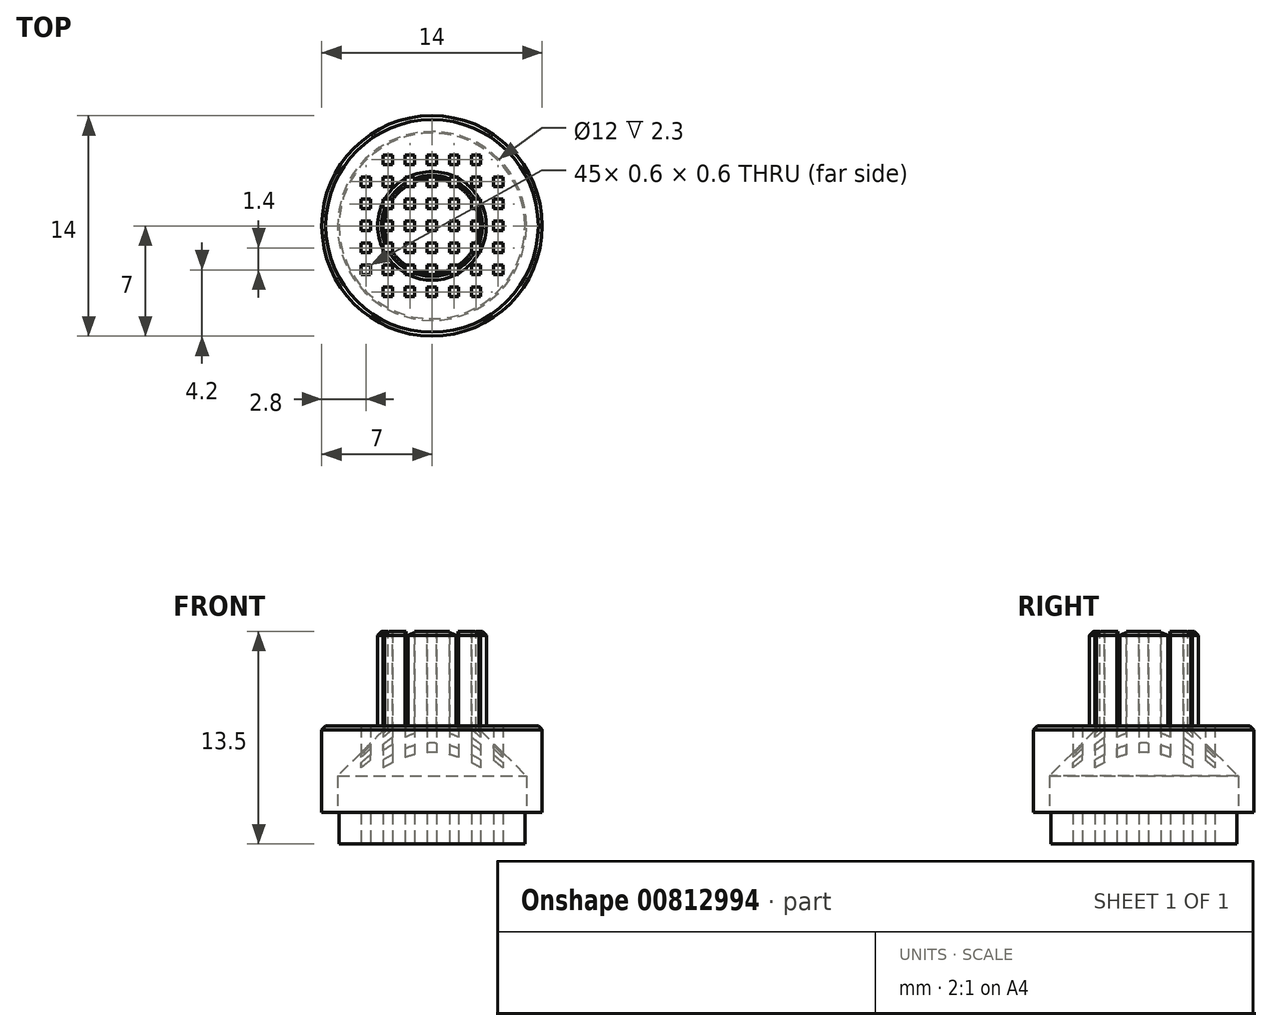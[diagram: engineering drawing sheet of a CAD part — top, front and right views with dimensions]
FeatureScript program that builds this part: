
annotation { "Feature Type Name" : "Feature", "Feature Type Description" : "" }
export const myFeature = defineFeature(function(context is Context, id is Id, definition is map)
    precondition{}
    {
        {
            var Q0;
            Q0=qCreatedBy(makeId("Top.planeOp"),FACE);
            var sketch = newSketch(context, id + "F0", { "sketchPlane" : qUnion([Q0])});
            skCircle(sketch, "E0", {"center": v(0, 0) * mm, "radius": 7 * mm});
            skSolve(sketch);
        }
        {
            var Q0;
            Q0 = qSketchRegion(id + "F0", true);
            extrude(context, id + "F1", {"entities" : qUnion([Q0]), "depth" : 5.5 * mm, "offsetDistance" : 25 * mm});
        }
        {
            var Q0;
            Q0=makeQuery(id+"F1.opExtrude","CAP_FACE",FACE,{"disambiguationData":[OSD([sQuery(id+"F0.wireOp",EDGE,"E0")])],"isStart":false});
            var sketch = newSketch(context, id + "F2", { "sketchPlane" : qUnion([Q0])});
            skCircle(sketch, "E1", {"center": v(0, 0) * mm, "radius": 3.45 * mm});
            skSolve(sketch);
        }
        {
            var Q0;
            Q0=makeQuery(id+"F2.imprint","IMPRINT",FACE,{"disambiguationData":[TD([[makeQuery(id+"F2.imprint","IMPRINT",EDGE,{"derivedFrom":sQuery(id+"F2.wireOp",EDGE,"E1")}),1.0]])]});
            extrude(context, id + "F3", {"entities" : qUnion([Q0]), "operationType" : NewBodyOperationType.ADD, "depth" : 6 * mm, "offsetDistance" : 25 * mm});
        }
        {
            var Q0;
            Q0=makeQuery(id+"F3.opExtrude","CAP_FACE",FACE,{"disambiguationData":[OSD([sQuery(id+"F2.wireOp",EDGE,"E1")])],"isStart":false});
            var sketch = newSketch(context, id + "F4", { "sketchPlane" : qUnion([Q0])});
            skCircle(sketch, "E2", {"center": v(0, 0) * mm, "radius": 3 * mm});
            skSolve(sketch);
        }
        {
            var Q0;
            Q0=makeQuery(id+"F4.imprint","IMPRINT",FACE,{"disambiguationData":[TD([[makeQuery(id+"F4.imprint","IMPRINT",EDGE,{"derivedFrom":sQuery(id+"F4.wireOp",EDGE,"E2")}),1.0]])]});
            extrude(context, id + "F5", {"entities" : qUnion([Q0]), "operationType" : NewBodyOperationType.REMOVE, "oppositeDirection" : true, "depth" : 25 * mm, "offsetDistance" : 25 * mm});
        }
        {
            var Q0;
            Q0=makeQuery(id+"F1.opExtrude","CAP_FACE",FACE,{"disambiguationData":[OSD([sQuery(id+"F0.wireOp",EDGE,"E0")])],"isStart":true});
            var sketch = newSketch(context, id + "F6", { "sketchPlane" : qUnion([Q0])});
            skCircle(sketch, "E3", {"center": v(0, 0) * mm, "radius": 6 * mm});
            skSolve(sketch);
        }
        {
            var Q0;
            Q0=makeQuery(id+"F6.imprint","IMPRINT",FACE,{"disambiguationData":[TD([[makeQuery(id+"F6.imprint","IMPRINT",EDGE,{"derivedFrom":makeQuery(id+"F5.boolean.opBoolean","INTERSECT",EDGE,{"derivedFrom":[makeQuery(id+"F1.opExtrude","CAP_FACE",FACE,{"disambiguationData":[OSD([sQuery(id+"F0.wireOp",EDGE,"E0")])],"isStart":true}),makeQuery(id+"F5.opExtrude","SWEPT_FACE",FACE,{"disambiguationData":[OSD([sQuery(id+"F4.wireOp",EDGE,"E2")])]})]})}),-1.0]])]});
            var Q1;
            Q1=makeQuery(id+"F6.imprint","IMPRINT",FACE,{"disambiguationData":[TD([[makeQuery(id+"F6.imprint","IMPRINT",EDGE,{"derivedFrom":sQuery(id+"F6.wireOp",EDGE,"E3")}),1.0]])]});
            extrude(context, id + "F7", {"entities" : qUnion([Q0, Q1]), "operationType" : NewBodyOperationType.REMOVE, "oppositeDirection" : true, "depth" : 2 * mm, "offsetDistance" : 25 * mm});
        }
        {
            var Q0;
            Q0=makeQuery(id+"F7.boolean.opBoolean","INTERSECT",EDGE,{"derivedFrom":[makeQuery(id+"F5.boolean.opBoolean","COPY",FACE,{"derivedFrom":makeQuery(id+"F5.opExtrude","SWEPT_FACE",FACE,{"disambiguationData":[OSD([sQuery(id+"F4.wireOp",EDGE,"E2")])]})}),makeQuery(id+"F7.opExtrude","CAP_FACE",FACE,{"disambiguationData":[OSD([sQuery(id+"F6.wireOp",EDGE,"E3")])],"isStart":false})]});
            chamfer(context, id + "F8", {"entities" : qUnion([Q0]), "width" : 3.3 * mm, "tangentPropagation" : true});
        }
        {
            var Q0;
            Q0=makeQuery(id+"F3.opExtrude","CAP_EDGE",EDGE,{"disambiguationData":[OSD([sQuery(id+"F2.wireOp",EDGE,"E1")])],"isStart":false});
            var Q1;
            Q1=makeQuery(id+"F1.opExtrude","CAP_EDGE",EDGE,{"disambiguationData":[OSD([sQuery(id+"F0.wireOp",EDGE,"E0")])],"isStart":false});
            chamfer(context, id + "F9", {"entities" : qUnion([Q0, Q1]), "width" : 0.25 * mm, "tangentPropagation" : true});
        }
        {
            var Q0;
            Q0=qCreatedBy(makeId("Top.planeOp"),FACE);
            var sketch = newSketch(context, id + "F10", { "sketchPlane" : qUnion([Q0])});
            skCircle(sketch, "E4", {"center": v(0, 0) * mm, "radius": 5.9 * mm});
            skSolve(sketch);
        }
        {
            var Q0;
            Q0=makeQuery(id+"F10.imprint","IMPRINT",FACE,{"disambiguationData":[TD([[makeQuery(id+"F10.imprint","IMPRINT",EDGE,{"derivedFrom":sQuery(id+"F10.wireOp",EDGE,"E4")}),1.0]])]});
            extrude(context, id + "F11", {"entities" : qUnion([Q0]), "operationType" : NewBodyOperationType.ADD, "oppositeDirection" : true, "depth" : 2 * mm, "offsetDistance" : 25 * mm});
        }
        {
            var Q0;
            Q0=makeQuery(id+"F11.opExtrude","CAP_FACE",FACE,{"disambiguationData":[OSD([sQuery(id+"F10.wireOp",EDGE,"E4")])],"isStart":false});
            var sketch = newSketch(context, id + "F12", { "sketchPlane" : qUnion([Q0])});
            skLineSegment(sketch, "E5.bottom", {"start": v(-5.3, -5.9) * mm, "end": v(-5.9, -5.9) * mm});
            skLineSegment(sketch, "E5.top", {"start": v(-5.3, -5.3) * mm, "end": v(-5.9, -5.3) * mm});
            skLineSegment(sketch, "E5.left", {"start": v(-5.3, -5.9) * mm, "end": v(-5.3, -5.3) * mm});
            skLineSegment(sketch, "E5.right", {"start": v(-5.9, -5.9) * mm, "end": v(-5.9, -5.3) * mm});
            skPoint(sketch, "E5.middle", {"position": v(-5.6, -5.6) * mm});
            skPoint(sketch, "E6.1.2.0", {"position": v(-4.2, -2.8) * mm});
            skLineSegment(sketch, "E6.1.2.1", {"start": v(-3.9, -3.1) * mm, "end": v(-4.5, -3.1) * mm});
            skLineSegment(sketch, "E6.1.2.2", {"start": v(-3.9, -2.5) * mm, "end": v(-4.5, -2.5) * mm});
            skLineSegment(sketch, "E6.1.2.3", {"start": v(-3.9, -3.1) * mm, "end": v(-3.9, -2.5) * mm});
            skLineSegment(sketch, "E6.1.2.4", {"start": v(-4.5, -3.1) * mm, "end": v(-4.5, -2.5) * mm});
            skPoint(sketch, "E6.1.3.0", {"position": v(-4.2, -1.4) * mm});
            skLineSegment(sketch, "E6.1.3.1", {"start": v(-3.9, -1.7) * mm, "end": v(-4.5, -1.7) * mm});
            skLineSegment(sketch, "E6.1.3.2", {"start": v(-3.9, -1.1) * mm, "end": v(-4.5, -1.1) * mm});
            skLineSegment(sketch, "E6.1.3.3", {"start": v(-3.9, -1.7) * mm, "end": v(-3.9, -1.1) * mm});
            skLineSegment(sketch, "E6.1.3.4", {"start": v(-4.5, -1.7) * mm, "end": v(-4.5, -1.1) * mm});
            skPoint(sketch, "E6.1.4.0", {"position": v(-4.2, 0) * mm});
            skLineSegment(sketch, "E6.1.4.1", {"start": v(-3.9, -0.3) * mm, "end": v(-4.5, -0.3) * mm});
            skLineSegment(sketch, "E6.1.4.2", {"start": v(-3.9, 0.3) * mm, "end": v(-4.5, 0.3) * mm});
            skLineSegment(sketch, "E6.1.4.3", {"start": v(-3.9, -0.3) * mm, "end": v(-3.9, 0.3) * mm});
            skLineSegment(sketch, "E6.1.4.4", {"start": v(-4.5, -0.3) * mm, "end": v(-4.5, 0.3) * mm});
            skPoint(sketch, "E6.1.5.0", {"position": v(-4.2, 1.4) * mm});
            skLineSegment(sketch, "E6.1.5.1", {"start": v(-3.9, 1.1) * mm, "end": v(-4.5, 1.1) * mm});
            skLineSegment(sketch, "E6.1.5.2", {"start": v(-3.9, 1.7) * mm, "end": v(-4.5, 1.7) * mm});
            skLineSegment(sketch, "E6.1.5.3", {"start": v(-3.9, 1.1) * mm, "end": v(-3.9, 1.7) * mm});
            skLineSegment(sketch, "E6.1.5.4", {"start": v(-4.5, 1.1) * mm, "end": v(-4.5, 1.7) * mm});
            skPoint(sketch, "E6.1.6.0", {"position": v(-4.2, 2.8) * mm});
            skLineSegment(sketch, "E6.1.6.1", {"start": v(-3.9, 2.5) * mm, "end": v(-4.5, 2.5) * mm});
            skLineSegment(sketch, "E6.1.6.2", {"start": v(-3.9, 3.1) * mm, "end": v(-4.5, 3.1) * mm});
            skLineSegment(sketch, "E6.1.6.3", {"start": v(-3.9, 2.5) * mm, "end": v(-3.9, 3.1) * mm});
            skLineSegment(sketch, "E6.1.6.4", {"start": v(-4.5, 2.5) * mm, "end": v(-4.5, 3.1) * mm});
            skPoint(sketch, "E6.2.1.0", {"position": v(-2.8, -4.2) * mm});
            skLineSegment(sketch, "E6.2.1.1", {"start": v(-2.5, -4.5) * mm, "end": v(-3.1, -4.5) * mm});
            skLineSegment(sketch, "E6.2.1.2", {"start": v(-2.5, -3.9) * mm, "end": v(-3.1, -3.9) * mm});
            skLineSegment(sketch, "E6.2.1.3", {"start": v(-2.5, -4.5) * mm, "end": v(-2.5, -3.9) * mm});
            skLineSegment(sketch, "E6.2.1.4", {"start": v(-3.1, -4.5) * mm, "end": v(-3.1, -3.9) * mm});
            skPoint(sketch, "E6.2.2.0", {"position": v(-2.8, -2.8) * mm});
            skLineSegment(sketch, "E6.2.2.1", {"start": v(-2.5, -3.1) * mm, "end": v(-3.1, -3.1) * mm});
            skLineSegment(sketch, "E6.2.2.2", {"start": v(-2.5, -2.5) * mm, "end": v(-3.1, -2.5) * mm});
            skLineSegment(sketch, "E6.2.2.3", {"start": v(-2.5, -3.1) * mm, "end": v(-2.5, -2.5) * mm});
            skLineSegment(sketch, "E6.2.2.4", {"start": v(-3.1, -3.1) * mm, "end": v(-3.1, -2.5) * mm});
            skPoint(sketch, "E6.2.3.0", {"position": v(-2.8, -1.4) * mm});
            skLineSegment(sketch, "E6.2.3.1", {"start": v(-2.5, -1.7) * mm, "end": v(-3.1, -1.7) * mm});
            skLineSegment(sketch, "E6.2.3.2", {"start": v(-2.5, -1.1) * mm, "end": v(-3.1, -1.1) * mm});
            skLineSegment(sketch, "E6.2.3.3", {"start": v(-2.5, -1.7) * mm, "end": v(-2.5, -1.1) * mm});
            skLineSegment(sketch, "E6.2.3.4", {"start": v(-3.1, -1.7) * mm, "end": v(-3.1, -1.1) * mm});
            skPoint(sketch, "E6.2.4.0", {"position": v(-2.8, 0) * mm});
            skLineSegment(sketch, "E6.2.4.1", {"start": v(-2.5, -0.3) * mm, "end": v(-3.1, -0.3) * mm});
            skLineSegment(sketch, "E6.2.4.2", {"start": v(-2.5, 0.3) * mm, "end": v(-3.1, 0.3) * mm});
            skLineSegment(sketch, "E6.2.4.3", {"start": v(-2.5, -0.3) * mm, "end": v(-2.5, 0.3) * mm});
            skLineSegment(sketch, "E6.2.4.4", {"start": v(-3.1, -0.3) * mm, "end": v(-3.1, 0.3) * mm});
            skPoint(sketch, "E6.2.5.0", {"position": v(-2.8, 1.4) * mm});
            skLineSegment(sketch, "E6.2.5.1", {"start": v(-2.5, 1.1) * mm, "end": v(-3.1, 1.1) * mm});
            skLineSegment(sketch, "E6.2.5.2", {"start": v(-2.5, 1.7) * mm, "end": v(-3.1, 1.7) * mm});
            skLineSegment(sketch, "E6.2.5.3", {"start": v(-2.5, 1.1) * mm, "end": v(-2.5, 1.7) * mm});
            skLineSegment(sketch, "E6.2.5.4", {"start": v(-3.1, 1.1) * mm, "end": v(-3.1, 1.7) * mm});
            skPoint(sketch, "E6.2.6.0", {"position": v(-2.8, 2.8) * mm});
            skLineSegment(sketch, "E6.2.6.1", {"start": v(-2.5, 2.5) * mm, "end": v(-3.1, 2.5) * mm});
            skLineSegment(sketch, "E6.2.6.2", {"start": v(-2.5, 3.1) * mm, "end": v(-3.1, 3.1) * mm});
            skLineSegment(sketch, "E6.2.6.3", {"start": v(-2.5, 2.5) * mm, "end": v(-2.5, 3.1) * mm});
            skLineSegment(sketch, "E6.2.6.4", {"start": v(-3.1, 2.5) * mm, "end": v(-3.1, 3.1) * mm});
            skPoint(sketch, "E6.2.7.0", {"position": v(-2.8, 4.2) * mm});
            skLineSegment(sketch, "E6.2.7.1", {"start": v(-2.5, 3.9) * mm, "end": v(-3.1, 3.9) * mm});
            skLineSegment(sketch, "E6.2.7.2", {"start": v(-2.5, 4.5) * mm, "end": v(-3.1, 4.5) * mm});
            skLineSegment(sketch, "E6.2.7.3", {"start": v(-2.5, 3.9) * mm, "end": v(-2.5, 4.5) * mm});
            skLineSegment(sketch, "E6.2.7.4", {"start": v(-3.1, 3.9) * mm, "end": v(-3.1, 4.5) * mm});
            skPoint(sketch, "E6.3.1.0", {"position": v(-1.4, -4.2) * mm});
            skLineSegment(sketch, "E6.3.1.1", {"start": v(-1.1, -4.5) * mm, "end": v(-1.7, -4.5) * mm});
            skLineSegment(sketch, "E6.3.1.2", {"start": v(-1.1, -3.9) * mm, "end": v(-1.7, -3.9) * mm});
            skLineSegment(sketch, "E6.3.1.3", {"start": v(-1.1, -4.5) * mm, "end": v(-1.1, -3.9) * mm});
            skLineSegment(sketch, "E6.3.1.4", {"start": v(-1.7, -4.5) * mm, "end": v(-1.7, -3.9) * mm});
            skPoint(sketch, "E6.3.2.0", {"position": v(-1.4, -2.8) * mm});
            skLineSegment(sketch, "E6.3.2.1", {"start": v(-1.1, -3.1) * mm, "end": v(-1.7, -3.1) * mm});
            skLineSegment(sketch, "E6.3.2.2", {"start": v(-1.1, -2.5) * mm, "end": v(-1.7, -2.5) * mm});
            skLineSegment(sketch, "E6.3.2.3", {"start": v(-1.1, -3.1) * mm, "end": v(-1.1, -2.5) * mm});
            skLineSegment(sketch, "E6.3.2.4", {"start": v(-1.7, -3.1) * mm, "end": v(-1.7, -2.5) * mm});
            skPoint(sketch, "E6.3.3.0", {"position": v(-1.4, -1.4) * mm});
            skLineSegment(sketch, "E6.3.3.1", {"start": v(-1.1, -1.7) * mm, "end": v(-1.7, -1.7) * mm});
            skLineSegment(sketch, "E6.3.3.2", {"start": v(-1.1, -1.1) * mm, "end": v(-1.7, -1.1) * mm});
            skLineSegment(sketch, "E6.3.3.3", {"start": v(-1.1, -1.7) * mm, "end": v(-1.1, -1.1) * mm});
            skLineSegment(sketch, "E6.3.3.4", {"start": v(-1.7, -1.7) * mm, "end": v(-1.7, -1.1) * mm});
            skPoint(sketch, "E6.3.4.0", {"position": v(-1.4, 0) * mm});
            skLineSegment(sketch, "E6.3.4.1", {"start": v(-1.1, -0.3) * mm, "end": v(-1.7, -0.3) * mm});
            skLineSegment(sketch, "E6.3.4.2", {"start": v(-1.1, 0.3) * mm, "end": v(-1.7, 0.3) * mm});
            skLineSegment(sketch, "E6.3.4.3", {"start": v(-1.1, -0.3) * mm, "end": v(-1.1, 0.3) * mm});
            skLineSegment(sketch, "E6.3.4.4", {"start": v(-1.7, -0.3) * mm, "end": v(-1.7, 0.3) * mm});
            skPoint(sketch, "E6.3.5.0", {"position": v(-1.4, 1.4) * mm});
            skLineSegment(sketch, "E6.3.5.1", {"start": v(-1.1, 1.1) * mm, "end": v(-1.7, 1.1) * mm});
            skLineSegment(sketch, "E6.3.5.2", {"start": v(-1.1, 1.7) * mm, "end": v(-1.7, 1.7) * mm});
            skLineSegment(sketch, "E6.3.5.3", {"start": v(-1.1, 1.1) * mm, "end": v(-1.1, 1.7) * mm});
            skLineSegment(sketch, "E6.3.5.4", {"start": v(-1.7, 1.1) * mm, "end": v(-1.7, 1.7) * mm});
            skPoint(sketch, "E6.3.6.0", {"position": v(-1.4, 2.8) * mm});
            skLineSegment(sketch, "E6.3.6.1", {"start": v(-1.1, 2.5) * mm, "end": v(-1.7, 2.5) * mm});
            skLineSegment(sketch, "E6.3.6.2", {"start": v(-1.1, 3.1) * mm, "end": v(-1.7, 3.1) * mm});
            skLineSegment(sketch, "E6.3.6.3", {"start": v(-1.1, 2.5) * mm, "end": v(-1.1, 3.1) * mm});
            skLineSegment(sketch, "E6.3.6.4", {"start": v(-1.7, 2.5) * mm, "end": v(-1.7, 3.1) * mm});
            skPoint(sketch, "E6.3.7.0", {"position": v(-1.4, 4.2) * mm});
            skLineSegment(sketch, "E6.3.7.1", {"start": v(-1.1, 3.9) * mm, "end": v(-1.7, 3.9) * mm});
            skLineSegment(sketch, "E6.3.7.2", {"start": v(-1.1, 4.5) * mm, "end": v(-1.7, 4.5) * mm});
            skLineSegment(sketch, "E6.3.7.3", {"start": v(-1.1, 3.9) * mm, "end": v(-1.1, 4.5) * mm});
            skLineSegment(sketch, "E6.3.7.4", {"start": v(-1.7, 3.9) * mm, "end": v(-1.7, 4.5) * mm});
            skPoint(sketch, "E6.4.1.0", {"position": v(0, -4.2) * mm});
            skLineSegment(sketch, "E6.4.1.1", {"start": v(0.3, -4.5) * mm, "end": v(-0.3, -4.5) * mm});
            skLineSegment(sketch, "E6.4.1.2", {"start": v(0.3, -3.9) * mm, "end": v(-0.3, -3.9) * mm});
            skLineSegment(sketch, "E6.4.1.3", {"start": v(0.3, -4.5) * mm, "end": v(0.3, -3.9) * mm});
            skLineSegment(sketch, "E6.4.1.4", {"start": v(-0.3, -4.5) * mm, "end": v(-0.3, -3.9) * mm});
            skPoint(sketch, "E6.4.2.0", {"position": v(0, -2.8) * mm});
            skLineSegment(sketch, "E6.4.2.1", {"start": v(0.3, -3.1) * mm, "end": v(-0.3, -3.1) * mm});
            skLineSegment(sketch, "E6.4.2.2", {"start": v(0.3, -2.5) * mm, "end": v(-0.3, -2.5) * mm});
            skLineSegment(sketch, "E6.4.2.3", {"start": v(0.3, -3.1) * mm, "end": v(0.3, -2.5) * mm});
            skLineSegment(sketch, "E6.4.2.4", {"start": v(-0.3, -3.1) * mm, "end": v(-0.3, -2.5) * mm});
            skPoint(sketch, "E6.4.3.0", {"position": v(0, -1.4) * mm});
            skLineSegment(sketch, "E6.4.3.1", {"start": v(0.3, -1.7) * mm, "end": v(-0.3, -1.7) * mm});
            skLineSegment(sketch, "E6.4.3.2", {"start": v(0.3, -1.1) * mm, "end": v(-0.3, -1.1) * mm});
            skLineSegment(sketch, "E6.4.3.3", {"start": v(0.3, -1.7) * mm, "end": v(0.3, -1.1) * mm});
            skLineSegment(sketch, "E6.4.3.4", {"start": v(-0.3, -1.7) * mm, "end": v(-0.3, -1.1) * mm});
            skPoint(sketch, "E6.4.4.0", {"position": v(0, 0) * mm});
            skLineSegment(sketch, "E6.4.4.1", {"start": v(0.3, -0.3) * mm, "end": v(-0.3, -0.3) * mm});
            skLineSegment(sketch, "E6.4.4.2", {"start": v(0.3, 0.3) * mm, "end": v(-0.3, 0.3) * mm});
            skLineSegment(sketch, "E6.4.4.3", {"start": v(0.3, -0.3) * mm, "end": v(0.3, 0.3) * mm});
            skLineSegment(sketch, "E6.4.4.4", {"start": v(-0.3, -0.3) * mm, "end": v(-0.3, 0.3) * mm});
            skPoint(sketch, "E6.4.5.0", {"position": v(0, 1.4) * mm});
            skLineSegment(sketch, "E6.4.5.1", {"start": v(0.3, 1.1) * mm, "end": v(-0.3, 1.1) * mm});
            skLineSegment(sketch, "E6.4.5.2", {"start": v(0.3, 1.7) * mm, "end": v(-0.3, 1.7) * mm});
            skLineSegment(sketch, "E6.4.5.3", {"start": v(0.3, 1.1) * mm, "end": v(0.3, 1.7) * mm});
            skLineSegment(sketch, "E6.4.5.4", {"start": v(-0.3, 1.1) * mm, "end": v(-0.3, 1.7) * mm});
            skPoint(sketch, "E6.4.6.0", {"position": v(0, 2.8) * mm});
            skLineSegment(sketch, "E6.4.6.1", {"start": v(0.3, 2.5) * mm, "end": v(-0.3, 2.5) * mm});
            skLineSegment(sketch, "E6.4.6.2", {"start": v(0.3, 3.1) * mm, "end": v(-0.3, 3.1) * mm});
            skLineSegment(sketch, "E6.4.6.3", {"start": v(0.3, 2.5) * mm, "end": v(0.3, 3.1) * mm});
            skLineSegment(sketch, "E6.4.6.4", {"start": v(-0.3, 2.5) * mm, "end": v(-0.3, 3.1) * mm});
            skPoint(sketch, "E6.4.7.0", {"position": v(0, 4.2) * mm});
            skLineSegment(sketch, "E6.4.7.1", {"start": v(0.3, 3.9) * mm, "end": v(-0.3, 3.9) * mm});
            skLineSegment(sketch, "E6.4.7.2", {"start": v(0.3, 4.5) * mm, "end": v(-0.3, 4.5) * mm});
            skLineSegment(sketch, "E6.4.7.3", {"start": v(0.3, 3.9) * mm, "end": v(0.3, 4.5) * mm});
            skLineSegment(sketch, "E6.4.7.4", {"start": v(-0.3, 3.9) * mm, "end": v(-0.3, 4.5) * mm});
            skPoint(sketch, "E6.5.1.0", {"position": v(1.4, -4.2) * mm});
            skLineSegment(sketch, "E6.5.1.1", {"start": v(1.7, -4.5) * mm, "end": v(1.1, -4.5) * mm});
            skLineSegment(sketch, "E6.5.1.2", {"start": v(1.7, -3.9) * mm, "end": v(1.1, -3.9) * mm});
            skLineSegment(sketch, "E6.5.1.3", {"start": v(1.7, -4.5) * mm, "end": v(1.7, -3.9) * mm});
            skLineSegment(sketch, "E6.5.1.4", {"start": v(1.1, -4.5) * mm, "end": v(1.1, -3.9) * mm});
            skPoint(sketch, "E6.5.2.0", {"position": v(1.4, -2.8) * mm});
            skLineSegment(sketch, "E6.5.2.1", {"start": v(1.7, -3.1) * mm, "end": v(1.1, -3.1) * mm});
            skLineSegment(sketch, "E6.5.2.2", {"start": v(1.7, -2.5) * mm, "end": v(1.1, -2.5) * mm});
            skLineSegment(sketch, "E6.5.2.3", {"start": v(1.7, -3.1) * mm, "end": v(1.7, -2.5) * mm});
            skLineSegment(sketch, "E6.5.2.4", {"start": v(1.1, -3.1) * mm, "end": v(1.1, -2.5) * mm});
            skPoint(sketch, "E6.5.3.0", {"position": v(1.4, -1.4) * mm});
            skLineSegment(sketch, "E6.5.3.1", {"start": v(1.7, -1.7) * mm, "end": v(1.1, -1.7) * mm});
            skLineSegment(sketch, "E6.5.3.2", {"start": v(1.7, -1.1) * mm, "end": v(1.1, -1.1) * mm});
            skLineSegment(sketch, "E6.5.3.3", {"start": v(1.7, -1.7) * mm, "end": v(1.7, -1.1) * mm});
            skLineSegment(sketch, "E6.5.3.4", {"start": v(1.1, -1.7) * mm, "end": v(1.1, -1.1) * mm});
            skPoint(sketch, "E6.5.4.0", {"position": v(1.4, 0) * mm});
            skLineSegment(sketch, "E6.5.4.1", {"start": v(1.7, -0.3) * mm, "end": v(1.1, -0.3) * mm});
            skLineSegment(sketch, "E6.5.4.2", {"start": v(1.7, 0.3) * mm, "end": v(1.1, 0.3) * mm});
            skLineSegment(sketch, "E6.5.4.3", {"start": v(1.7, -0.3) * mm, "end": v(1.7, 0.3) * mm});
            skLineSegment(sketch, "E6.5.4.4", {"start": v(1.1, -0.3) * mm, "end": v(1.1, 0.3) * mm});
            skPoint(sketch, "E6.5.5.0", {"position": v(1.4, 1.4) * mm});
            skLineSegment(sketch, "E6.5.5.1", {"start": v(1.7, 1.1) * mm, "end": v(1.1, 1.1) * mm});
            skLineSegment(sketch, "E6.5.5.2", {"start": v(1.7, 1.7) * mm, "end": v(1.1, 1.7) * mm});
            skLineSegment(sketch, "E6.5.5.3", {"start": v(1.7, 1.1) * mm, "end": v(1.7, 1.7) * mm});
            skLineSegment(sketch, "E6.5.5.4", {"start": v(1.1, 1.1) * mm, "end": v(1.1, 1.7) * mm});
            skPoint(sketch, "E6.5.6.0", {"position": v(1.4, 2.8) * mm});
            skLineSegment(sketch, "E6.5.6.1", {"start": v(1.7, 2.5) * mm, "end": v(1.1, 2.5) * mm});
            skLineSegment(sketch, "E6.5.6.2", {"start": v(1.7, 3.1) * mm, "end": v(1.1, 3.1) * mm});
            skLineSegment(sketch, "E6.5.6.3", {"start": v(1.7, 2.5) * mm, "end": v(1.7, 3.1) * mm});
            skLineSegment(sketch, "E6.5.6.4", {"start": v(1.1, 2.5) * mm, "end": v(1.1, 3.1) * mm});
            skPoint(sketch, "E6.5.7.0", {"position": v(1.4, 4.2) * mm});
            skLineSegment(sketch, "E6.5.7.1", {"start": v(1.7, 3.9) * mm, "end": v(1.1, 3.9) * mm});
            skLineSegment(sketch, "E6.5.7.2", {"start": v(1.7, 4.5) * mm, "end": v(1.1, 4.5) * mm});
            skLineSegment(sketch, "E6.5.7.3", {"start": v(1.7, 3.9) * mm, "end": v(1.7, 4.5) * mm});
            skLineSegment(sketch, "E6.5.7.4", {"start": v(1.1, 3.9) * mm, "end": v(1.1, 4.5) * mm});
            skPoint(sketch, "E6.6.1.0", {"position": v(2.8, -4.2) * mm});
            skLineSegment(sketch, "E6.6.1.1", {"start": v(3.1, -4.5) * mm, "end": v(2.5, -4.5) * mm});
            skLineSegment(sketch, "E6.6.1.2", {"start": v(3.1, -3.9) * mm, "end": v(2.5, -3.9) * mm});
            skLineSegment(sketch, "E6.6.1.3", {"start": v(3.1, -4.5) * mm, "end": v(3.1, -3.9) * mm});
            skLineSegment(sketch, "E6.6.1.4", {"start": v(2.5, -4.5) * mm, "end": v(2.5, -3.9) * mm});
            skPoint(sketch, "E6.6.2.0", {"position": v(2.8, -2.8) * mm});
            skLineSegment(sketch, "E6.6.2.1", {"start": v(3.1, -3.1) * mm, "end": v(2.5, -3.1) * mm});
            skLineSegment(sketch, "E6.6.2.2", {"start": v(3.1, -2.5) * mm, "end": v(2.5, -2.5) * mm});
            skLineSegment(sketch, "E6.6.2.3", {"start": v(3.1, -3.1) * mm, "end": v(3.1, -2.5) * mm});
            skLineSegment(sketch, "E6.6.2.4", {"start": v(2.5, -3.1) * mm, "end": v(2.5, -2.5) * mm});
            skPoint(sketch, "E6.6.3.0", {"position": v(2.8, -1.4) * mm});
            skLineSegment(sketch, "E6.6.3.1", {"start": v(3.1, -1.7) * mm, "end": v(2.5, -1.7) * mm});
            skLineSegment(sketch, "E6.6.3.2", {"start": v(3.1, -1.1) * mm, "end": v(2.5, -1.1) * mm});
            skLineSegment(sketch, "E6.6.3.3", {"start": v(3.1, -1.7) * mm, "end": v(3.1, -1.1) * mm});
            skLineSegment(sketch, "E6.6.3.4", {"start": v(2.5, -1.7) * mm, "end": v(2.5, -1.1) * mm});
            skPoint(sketch, "E6.6.4.0", {"position": v(2.8, 0) * mm});
            skLineSegment(sketch, "E6.6.4.1", {"start": v(3.1, -0.3) * mm, "end": v(2.5, -0.3) * mm});
            skLineSegment(sketch, "E6.6.4.2", {"start": v(3.1, 0.3) * mm, "end": v(2.5, 0.3) * mm});
            skLineSegment(sketch, "E6.6.4.3", {"start": v(3.1, -0.3) * mm, "end": v(3.1, 0.3) * mm});
            skLineSegment(sketch, "E6.6.4.4", {"start": v(2.5, -0.3) * mm, "end": v(2.5, 0.3) * mm});
            skPoint(sketch, "E6.6.5.0", {"position": v(2.8, 1.4) * mm});
            skLineSegment(sketch, "E6.6.5.1", {"start": v(3.1, 1.1) * mm, "end": v(2.5, 1.1) * mm});
            skLineSegment(sketch, "E6.6.5.2", {"start": v(3.1, 1.7) * mm, "end": v(2.5, 1.7) * mm});
            skLineSegment(sketch, "E6.6.5.3", {"start": v(3.1, 1.1) * mm, "end": v(3.1, 1.7) * mm});
            skLineSegment(sketch, "E6.6.5.4", {"start": v(2.5, 1.1) * mm, "end": v(2.5, 1.7) * mm});
            skPoint(sketch, "E6.6.6.0", {"position": v(2.8, 2.8) * mm});
            skLineSegment(sketch, "E6.6.6.1", {"start": v(3.1, 2.5) * mm, "end": v(2.5, 2.5) * mm});
            skLineSegment(sketch, "E6.6.6.2", {"start": v(3.1, 3.1) * mm, "end": v(2.5, 3.1) * mm});
            skLineSegment(sketch, "E6.6.6.3", {"start": v(3.1, 2.5) * mm, "end": v(3.1, 3.1) * mm});
            skLineSegment(sketch, "E6.6.6.4", {"start": v(2.5, 2.5) * mm, "end": v(2.5, 3.1) * mm});
            skPoint(sketch, "E6.6.7.0", {"position": v(2.8, 4.2) * mm});
            skLineSegment(sketch, "E6.6.7.1", {"start": v(3.1, 3.9) * mm, "end": v(2.5, 3.9) * mm});
            skLineSegment(sketch, "E6.6.7.2", {"start": v(3.1, 4.5) * mm, "end": v(2.5, 4.5) * mm});
            skLineSegment(sketch, "E6.6.7.3", {"start": v(3.1, 3.9) * mm, "end": v(3.1, 4.5) * mm});
            skLineSegment(sketch, "E6.6.7.4", {"start": v(2.5, 3.9) * mm, "end": v(2.5, 4.5) * mm});
            skPoint(sketch, "E6.7.2.0", {"position": v(4.2, -2.8) * mm});
            skLineSegment(sketch, "E6.7.2.1", {"start": v(4.5, -3.1) * mm, "end": v(3.9, -3.1) * mm});
            skLineSegment(sketch, "E6.7.2.2", {"start": v(4.5, -2.5) * mm, "end": v(3.9, -2.5) * mm});
            skLineSegment(sketch, "E6.7.2.3", {"start": v(4.5, -3.1) * mm, "end": v(4.5, -2.5) * mm});
            skLineSegment(sketch, "E6.7.2.4", {"start": v(3.9, -3.1) * mm, "end": v(3.9, -2.5) * mm});
            skPoint(sketch, "E6.7.3.0", {"position": v(4.2, -1.4) * mm});
            skLineSegment(sketch, "E6.7.3.1", {"start": v(4.5, -1.7) * mm, "end": v(3.9, -1.7) * mm});
            skLineSegment(sketch, "E6.7.3.2", {"start": v(4.5, -1.1) * mm, "end": v(3.9, -1.1) * mm});
            skLineSegment(sketch, "E6.7.3.3", {"start": v(4.5, -1.7) * mm, "end": v(4.5, -1.1) * mm});
            skLineSegment(sketch, "E6.7.3.4", {"start": v(3.9, -1.7) * mm, "end": v(3.9, -1.1) * mm});
            skPoint(sketch, "E6.7.4.0", {"position": v(4.2, 0) * mm});
            skLineSegment(sketch, "E6.7.4.1", {"start": v(4.5, -0.3) * mm, "end": v(3.9, -0.3) * mm});
            skLineSegment(sketch, "E6.7.4.2", {"start": v(4.5, 0.3) * mm, "end": v(3.9, 0.3) * mm});
            skLineSegment(sketch, "E6.7.4.3", {"start": v(4.5, -0.3) * mm, "end": v(4.5, 0.3) * mm});
            skLineSegment(sketch, "E6.7.4.4", {"start": v(3.9, -0.3) * mm, "end": v(3.9, 0.3) * mm});
            skPoint(sketch, "E6.7.5.0", {"position": v(4.2, 1.4) * mm});
            skLineSegment(sketch, "E6.7.5.1", {"start": v(4.5, 1.1) * mm, "end": v(3.9, 1.1) * mm});
            skLineSegment(sketch, "E6.7.5.2", {"start": v(4.5, 1.7) * mm, "end": v(3.9, 1.7) * mm});
            skLineSegment(sketch, "E6.7.5.3", {"start": v(4.5, 1.1) * mm, "end": v(4.5, 1.7) * mm});
            skLineSegment(sketch, "E6.7.5.4", {"start": v(3.9, 1.1) * mm, "end": v(3.9, 1.7) * mm});
            skPoint(sketch, "E6.7.6.0", {"position": v(4.2, 2.8) * mm});
            skLineSegment(sketch, "E6.7.6.1", {"start": v(4.5, 2.5) * mm, "end": v(3.9, 2.5) * mm});
            skLineSegment(sketch, "E6.7.6.2", {"start": v(4.5, 3.1) * mm, "end": v(3.9, 3.1) * mm});
            skLineSegment(sketch, "E6.7.6.3", {"start": v(4.5, 2.5) * mm, "end": v(4.5, 3.1) * mm});
            skLineSegment(sketch, "E6.7.6.4", {"start": v(3.9, 2.5) * mm, "end": v(3.9, 3.1) * mm});
            skLineSegment(sketch, "E6.direction2", {"start": v(-5.9, -3.9) * mm, "end": v(-5.9, -5.3) * mm, "construction": true});
            skSolve(sketch);
        }
        {
            var Q0;
            Q0=makeQuery(id+"F12.imprint","IMPRINT",FACE,{"disambiguationData":[TD([[makeQuery(id+"F12.imprint","IMPRINT",EDGE,{"derivedFrom":sQuery(id+"F12.wireOp",EDGE,"E6.2.5.1")}),-1.0]])]});
            var Q1;
            Q1=makeQuery(id+"F12.imprint","IMPRINT",FACE,{"disambiguationData":[TD([[makeQuery(id+"F12.imprint","IMPRINT",EDGE,{"derivedFrom":sQuery(id+"F12.wireOp",EDGE,"E6.2.6.1")}),-1.0]])]});
            var Q2;
            Q2=makeQuery(id+"F12.imprint","IMPRINT",FACE,{"disambiguationData":[TD([[makeQuery(id+"F12.imprint","IMPRINT",EDGE,{"derivedFrom":sQuery(id+"F12.wireOp",EDGE,"E6.2.7.1")}),-1.0]])]});
            var Q3;
            Q3=makeQuery(id+"F12.imprint","IMPRINT",FACE,{"disambiguationData":[TD([[makeQuery(id+"F12.imprint","IMPRINT",EDGE,{"derivedFrom":sQuery(id+"F12.wireOp",EDGE,"E6.3.7.1")}),-1.0]])]});
            var Q4;
            Q4=makeQuery(id+"F12.imprint","IMPRINT",FACE,{"disambiguationData":[TD([[makeQuery(id+"F12.imprint","IMPRINT",EDGE,{"derivedFrom":sQuery(id+"F12.wireOp",EDGE,"E6.4.7.1")}),-1.0]])]});
            var Q5;
            Q5=makeQuery(id+"F12.imprint","IMPRINT",FACE,{"disambiguationData":[TD([[makeQuery(id+"F12.imprint","IMPRINT",EDGE,{"derivedFrom":sQuery(id+"F12.wireOp",EDGE,"E6.5.7.1")}),-1.0]])]});
            var Q6;
            Q6=makeQuery(id+"F12.imprint","IMPRINT",FACE,{"disambiguationData":[TD([[makeQuery(id+"F12.imprint","IMPRINT",EDGE,{"derivedFrom":sQuery(id+"F12.wireOp",EDGE,"E6.1.6.1")}),-1.0]])]});
            var Q7;
            Q7=makeQuery(id+"F12.imprint","IMPRINT",FACE,{"disambiguationData":[TD([[makeQuery(id+"F12.imprint","IMPRINT",EDGE,{"derivedFrom":sQuery(id+"F12.wireOp",EDGE,"E6.1.5.1")}),-1.0]])]});
            var Q8;
            Q8=makeQuery(id+"F12.imprint","IMPRINT",FACE,{"disambiguationData":[TD([[makeQuery(id+"F12.imprint","IMPRINT",EDGE,{"derivedFrom":sQuery(id+"F12.wireOp",EDGE,"E6.1.4.1")}),-1.0]])]});
            var Q9;
            Q9=makeQuery(id+"F12.imprint","IMPRINT",FACE,{"disambiguationData":[TD([[makeQuery(id+"F12.imprint","IMPRINT",EDGE,{"derivedFrom":sQuery(id+"F12.wireOp",EDGE,"E6.1.3.1")}),-1.0]])]});
            var Q10;
            Q10=makeQuery(id+"F12.imprint","IMPRINT",FACE,{"disambiguationData":[TD([[makeQuery(id+"F12.imprint","IMPRINT",EDGE,{"derivedFrom":sQuery(id+"F12.wireOp",EDGE,"E6.1.2.1")}),-1.0]])]});
            var Q11;
            Q11=makeQuery(id+"F12.imprint","IMPRINT",FACE,{"disambiguationData":[TD([[makeQuery(id+"F12.imprint","IMPRINT",EDGE,{"derivedFrom":sQuery(id+"F12.wireOp",EDGE,"E6.2.2.1")}),-1.0]])]});
            var Q12;
            Q12=makeQuery(id+"F12.imprint","IMPRINT",FACE,{"disambiguationData":[TD([[makeQuery(id+"F12.imprint","IMPRINT",EDGE,{"derivedFrom":sQuery(id+"F12.wireOp",EDGE,"E6.2.3.1")}),-1.0]])]});
            var Q13;
            Q13=makeQuery(id+"F12.imprint","IMPRINT",FACE,{"disambiguationData":[TD([[makeQuery(id+"F12.imprint","IMPRINT",EDGE,{"derivedFrom":sQuery(id+"F12.wireOp",EDGE,"E6.2.4.1")}),-1.0]])]});
            var Q14;
            Q14=makeQuery(id+"F12.imprint","IMPRINT",FACE,{"disambiguationData":[TD([[makeQuery(id+"F12.imprint","IMPRINT",EDGE,{"derivedFrom":sQuery(id+"F12.wireOp",EDGE,"E6.3.5.1")}),-1.0]])]});
            var Q15;
            Q15=makeQuery(id+"F12.imprint","IMPRINT",FACE,{"disambiguationData":[TD([[makeQuery(id+"F12.imprint","IMPRINT",EDGE,{"derivedFrom":sQuery(id+"F12.wireOp",EDGE,"E6.3.6.1")}),-1.0]])]});
            var Q16;
            Q16=makeQuery(id+"F12.imprint","IMPRINT",FACE,{"disambiguationData":[TD([[makeQuery(id+"F12.imprint","IMPRINT",EDGE,{"derivedFrom":sQuery(id+"F12.wireOp",EDGE,"E6.4.6.1")}),-1.0]])]});
            var Q17;
            Q17=makeQuery(id+"F12.imprint","IMPRINT",FACE,{"disambiguationData":[TD([[makeQuery(id+"F12.imprint","IMPRINT",EDGE,{"derivedFrom":sQuery(id+"F12.wireOp",EDGE,"E6.4.5.1")}),-1.0]])]});
            var Q18;
            Q18=makeQuery(id+"F12.imprint","IMPRINT",FACE,{"disambiguationData":[TD([[makeQuery(id+"F12.imprint","IMPRINT",EDGE,{"derivedFrom":sQuery(id+"F12.wireOp",EDGE,"E6.4.4.1")}),-1.0]])]});
            var Q19;
            Q19=makeQuery(id+"F12.imprint","IMPRINT",FACE,{"disambiguationData":[TD([[makeQuery(id+"F12.imprint","IMPRINT",EDGE,{"derivedFrom":sQuery(id+"F12.wireOp",EDGE,"E6.3.4.1")}),-1.0]])]});
            var Q20;
            Q20=makeQuery(id+"F12.imprint","IMPRINT",FACE,{"disambiguationData":[TD([[makeQuery(id+"F12.imprint","IMPRINT",EDGE,{"derivedFrom":sQuery(id+"F12.wireOp",EDGE,"E6.3.3.1")}),-1.0]])]});
            var Q21;
            Q21=makeQuery(id+"F12.imprint","IMPRINT",FACE,{"disambiguationData":[TD([[makeQuery(id+"F12.imprint","IMPRINT",EDGE,{"derivedFrom":sQuery(id+"F12.wireOp",EDGE,"E6.3.2.1")}),-1.0]])]});
            var Q22;
            Q22=makeQuery(id+"F12.imprint","IMPRINT",FACE,{"disambiguationData":[TD([[makeQuery(id+"F12.imprint","IMPRINT",EDGE,{"derivedFrom":sQuery(id+"F12.wireOp",EDGE,"E6.2.1.1")}),-1.0]])]});
            var Q23;
            Q23=makeQuery(id+"F12.imprint","IMPRINT",FACE,{"disambiguationData":[TD([[makeQuery(id+"F12.imprint","IMPRINT",EDGE,{"derivedFrom":sQuery(id+"F12.wireOp",EDGE,"E6.3.1.1")}),-1.0]])]});
            var Q24;
            Q24=makeQuery(id+"F12.imprint","IMPRINT",FACE,{"disambiguationData":[TD([[makeQuery(id+"F12.imprint","IMPRINT",EDGE,{"derivedFrom":sQuery(id+"F12.wireOp",EDGE,"E6.4.1.1")}),-1.0]])]});
            var Q25;
            Q25=makeQuery(id+"F12.imprint","IMPRINT",FACE,{"disambiguationData":[TD([[makeQuery(id+"F12.imprint","IMPRINT",EDGE,{"derivedFrom":sQuery(id+"F12.wireOp",EDGE,"E6.5.1.1")}),-1.0]])]});
            var Q26;
            Q26=makeQuery(id+"F12.imprint","IMPRINT",FACE,{"disambiguationData":[TD([[makeQuery(id+"F12.imprint","IMPRINT",EDGE,{"derivedFrom":sQuery(id+"F12.wireOp",EDGE,"E6.6.1.1")}),-1.0]])]});
            var Q27;
            Q27=makeQuery(id+"F12.imprint","IMPRINT",FACE,{"disambiguationData":[TD([[makeQuery(id+"F12.imprint","IMPRINT",EDGE,{"derivedFrom":sQuery(id+"F12.wireOp",EDGE,"E6.7.2.1")}),-1.0]])]});
            var Q28;
            Q28=makeQuery(id+"F12.imprint","IMPRINT",FACE,{"disambiguationData":[TD([[makeQuery(id+"F12.imprint","IMPRINT",EDGE,{"derivedFrom":sQuery(id+"F12.wireOp",EDGE,"E6.6.2.1")}),-1.0]])]});
            var Q29;
            Q29=makeQuery(id+"F12.imprint","IMPRINT",FACE,{"disambiguationData":[TD([[makeQuery(id+"F12.imprint","IMPRINT",EDGE,{"derivedFrom":sQuery(id+"F12.wireOp",EDGE,"E6.5.2.1")}),-1.0]])]});
            var Q30;
            Q30=makeQuery(id+"F12.imprint","IMPRINT",FACE,{"disambiguationData":[TD([[makeQuery(id+"F12.imprint","IMPRINT",EDGE,{"derivedFrom":sQuery(id+"F12.wireOp",EDGE,"E6.5.3.1")}),-1.0]])]});
            var Q31;
            Q31=makeQuery(id+"F12.imprint","IMPRINT",FACE,{"disambiguationData":[TD([[makeQuery(id+"F12.imprint","IMPRINT",EDGE,{"derivedFrom":sQuery(id+"F12.wireOp",EDGE,"E6.5.4.1")}),-1.0]])]});
            var Q32;
            Q32=makeQuery(id+"F12.imprint","IMPRINT",FACE,{"disambiguationData":[TD([[makeQuery(id+"F12.imprint","IMPRINT",EDGE,{"derivedFrom":sQuery(id+"F12.wireOp",EDGE,"E6.5.5.1")}),-1.0]])]});
            var Q33;
            Q33=makeQuery(id+"F12.imprint","IMPRINT",FACE,{"disambiguationData":[TD([[makeQuery(id+"F12.imprint","IMPRINT",EDGE,{"derivedFrom":sQuery(id+"F12.wireOp",EDGE,"E6.6.7.1")}),-1.0]])]});
            var Q34;
            Q34=makeQuery(id+"F12.imprint","IMPRINT",FACE,{"disambiguationData":[TD([[makeQuery(id+"F12.imprint","IMPRINT",EDGE,{"derivedFrom":sQuery(id+"F12.wireOp",EDGE,"E6.7.6.1")}),-1.0]])]});
            var Q35;
            Q35=makeQuery(id+"F12.imprint","IMPRINT",FACE,{"disambiguationData":[TD([[makeQuery(id+"F12.imprint","IMPRINT",EDGE,{"derivedFrom":sQuery(id+"F12.wireOp",EDGE,"E6.7.5.1")}),-1.0]])]});
            var Q36;
            Q36=makeQuery(id+"F12.imprint","IMPRINT",FACE,{"disambiguationData":[TD([[makeQuery(id+"F12.imprint","IMPRINT",EDGE,{"derivedFrom":sQuery(id+"F12.wireOp",EDGE,"E6.7.4.1")}),-1.0]])]});
            var Q37;
            Q37=makeQuery(id+"F12.imprint","IMPRINT",FACE,{"disambiguationData":[TD([[makeQuery(id+"F12.imprint","IMPRINT",EDGE,{"derivedFrom":sQuery(id+"F12.wireOp",EDGE,"E6.7.3.1")}),-1.0]])]});
            var Q38;
            Q38=makeQuery(id+"F12.imprint","IMPRINT",FACE,{"disambiguationData":[TD([[makeQuery(id+"F12.imprint","IMPRINT",EDGE,{"derivedFrom":sQuery(id+"F12.wireOp",EDGE,"E6.6.3.1")}),-1.0]])]});
            var Q39;
            Q39=makeQuery(id+"F12.imprint","IMPRINT",FACE,{"disambiguationData":[TD([[makeQuery(id+"F12.imprint","IMPRINT",EDGE,{"derivedFrom":sQuery(id+"F12.wireOp",EDGE,"E6.6.4.1")}),-1.0]])]});
            var Q40;
            Q40=makeQuery(id+"F12.imprint","IMPRINT",FACE,{"disambiguationData":[TD([[makeQuery(id+"F12.imprint","IMPRINT",EDGE,{"derivedFrom":sQuery(id+"F12.wireOp",EDGE,"E6.6.5.1")}),-1.0]])]});
            var Q41;
            Q41=makeQuery(id+"F12.imprint","IMPRINT",FACE,{"disambiguationData":[TD([[makeQuery(id+"F12.imprint","IMPRINT",EDGE,{"derivedFrom":sQuery(id+"F12.wireOp",EDGE,"E6.6.6.1")}),-1.0]])]});
            var Q42;
            Q42=makeQuery(id+"F12.imprint","IMPRINT",FACE,{"disambiguationData":[TD([[makeQuery(id+"F12.imprint","IMPRINT",EDGE,{"derivedFrom":sQuery(id+"F12.wireOp",EDGE,"E6.4.3.1")}),-1.0]])]});
            var Q43;
            Q43=makeQuery(id+"F12.imprint","IMPRINT",FACE,{"disambiguationData":[TD([[makeQuery(id+"F12.imprint","IMPRINT",EDGE,{"derivedFrom":sQuery(id+"F12.wireOp",EDGE,"E6.4.2.1")}),-1.0]])]});
            var Q44;
            Q44=makeQuery(id+"F12.imprint","IMPRINT",FACE,{"disambiguationData":[TD([[makeQuery(id+"F12.imprint","IMPRINT",EDGE,{"derivedFrom":sQuery(id+"F12.wireOp",EDGE,"E6.5.6.1")}),-1.0]])]});
            extrude(context, id + "F13", {"entities" : qUnion([Q0, Q1, Q2, Q3, Q4, Q5, Q6, Q7, Q8, Q9, Q10, Q11, Q12, Q13, Q14, Q15, Q16, Q17, Q18, Q19, Q20, Q21, Q22, Q23, Q24, Q25, Q26, Q27, Q28, Q29, Q30, Q31, Q32, Q33, Q34, Q35, Q36, Q37, Q38, Q39, Q40, Q41, Q42, Q43, Q44]), "operationType" : NewBodyOperationType.REMOVE, "oppositeDirection" : true, "depth" : 25 * mm, "offsetDistance" : 25 * mm});
        }
    });
